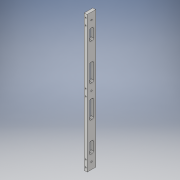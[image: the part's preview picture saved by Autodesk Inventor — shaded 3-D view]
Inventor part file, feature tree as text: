
AUTODESK INVENTOR PART (.ipt)
format: ipt  version: 2019 (Build 230136000, 136)  size: 211,456 bytes
history: native  units: in
note: dims shown in document units (in); Inventor stores cm internally (conversion verified against a paired STEP export)
features: fillet x16, sketch x4, extrude x2, hole x2
ambient origin geometry x8: Origin, YZ Plane, XZ Plane, XY Plane, X Axis, Y Axis, Z Axis, Center Point
bodies: Solid1 (feature_tree)
feature tree (24):
  extrude  "Extrusion1"  Depth=0.75in
  hole  "Hole1"  [1 undecoded]
  extrude  "Extrusion2"  Depth=5.9055in
  fillet  "Fillet1"  Radius=0.5906in
  fillet  "Fillet2"  Radius=0.375in
  fillet  "Fillet3"  Radius=0.375in
  fillet  "Fillet4"  Radius=5.9055in
  fillet  "Fillet5"  Radius=0.1969in
  fillet  "Fillet6"  Radius=0.1969in
  fillet  "Fillet7"  Radius=1.1811in
  fillet  "Fillet8"  Radius=1.1811in
  fillet  "Fillet9"  Radius=2.1654in
  fillet  "Fillet10"  Radius=3.7402in
  fillet  "Fillet11"  Radius=5.315in
  fillet  "Fillet12"  Radius=2.1654in
  fillet  "Fillet13"  Radius=3.7402in
  fillet  "Fillet14"  Radius=5.315in
  fillet  "Fillet15"  Radius=0.25in
  fillet  "Fillet16"  Radius=0.125in
  hole  "Hole3"  [1 undecoded]
  sketch  "Sketch1"  dims[d0=11.811in d1=0.75in]
  sketch  "Sketch2"  dims[d2=0.25in d3=0.0in d4=0.5906in]
  sketch  "Sketch5"  dims[d5=0.75in d6=0.375in d7=0.5906in d8=0.375in d9=0.375in d10=5.9055in]
  sketch  "Sketch7"  dims[d11=0.13in d12=0.328in d13=0.375in d14=0.25in d15=0.5635in d16=0.484in d17=0.8108in d44=0.1969in d45=0.1969in d46=1.1811in d47=1.1811in d48=2.1654in d49=3.7402in d50=5.315in d51=2.1654in d52=3.7402in d53=5.315in d54=0.25in d55=0.0in d56=0.125in d57=0.125in d58=0.125in d59=0.125in d60=0.125in d61=0.125in d62=0.125in d63=0.125in d64=0.125in d65=0.125in d66=0.125in d67=0.125in d68=0.125in d69=0.125in d70=0.125in d71=0.125in d72=0.2953in d73=0.8858in d74=5.6102in d78=0.2953in d79=0.8858in d82=5.6102in d83=0.25in d84=0.125in d85=0.125in d87=0.125in d88=0.125in d89=0.125in d91=0.125in d92=0.125in d93=0.125in d94=0.104in d95=1.0in d96=0.375in d97=0.25in d98=0.5635in d99=0.432in d100=0.0in]
note: 2 required parameter values undecoded (feature->parameter linkage not recoverable at this tier; creation-order binding heuristic only, values carry confidence <= 0.55)
